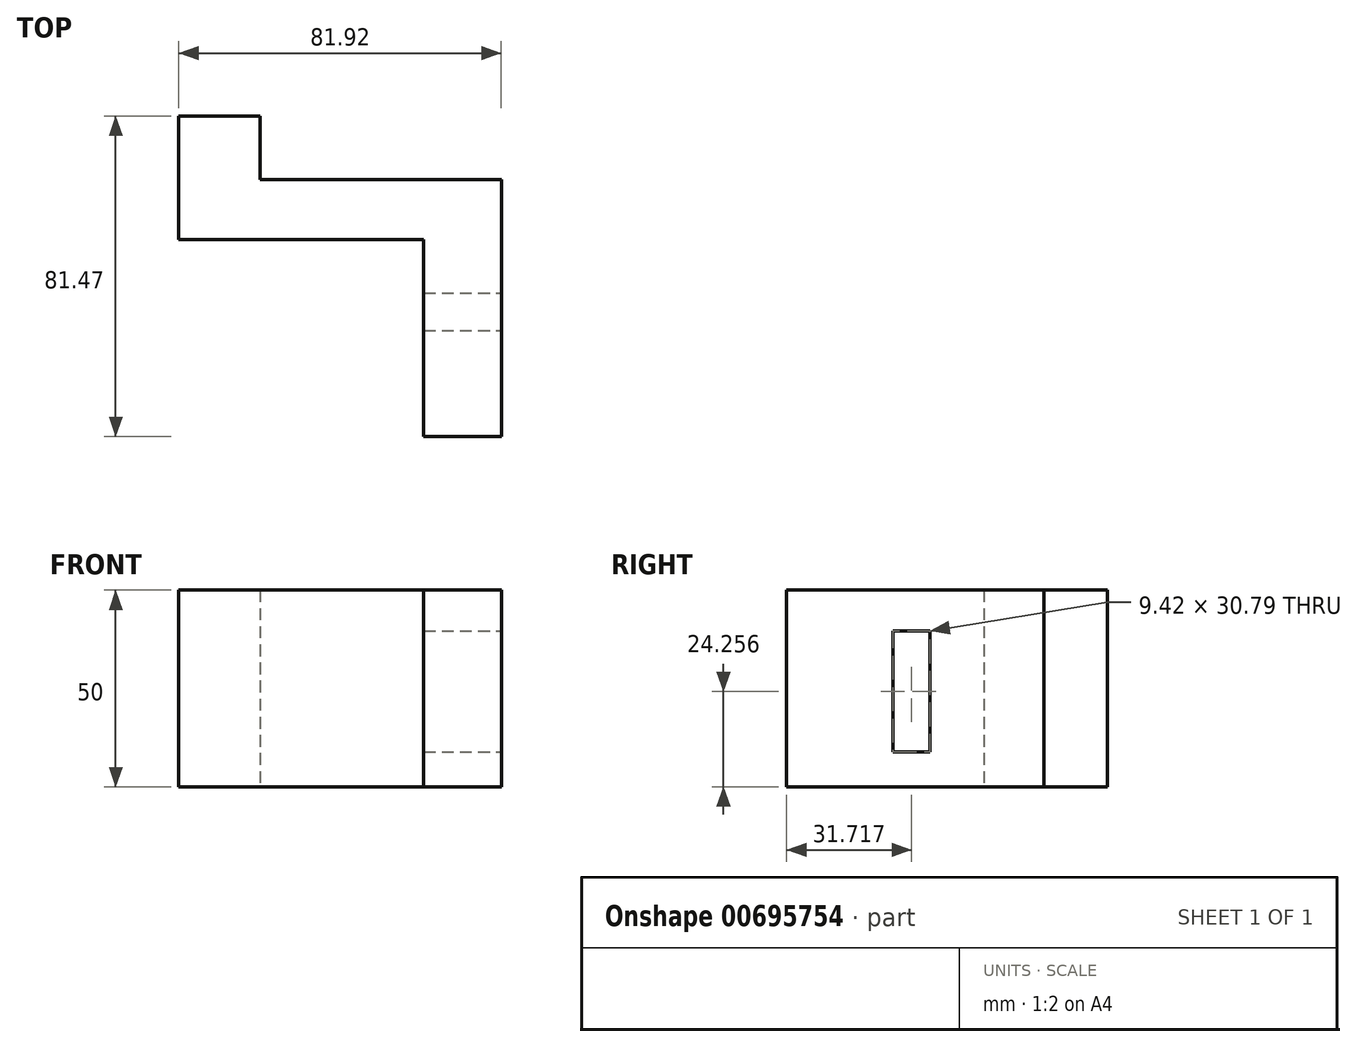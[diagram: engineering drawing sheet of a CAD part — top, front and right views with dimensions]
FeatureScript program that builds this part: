
annotation { "Feature Type Name" : "Feature", "Feature Type Description" : "" }
export const myFeature = defineFeature(function(context is Context, id is Id, definition is map)
    precondition{}
    {
        {
            var Q0;
            Q0=qCreatedBy(makeId("Top.planeOp"),FACE);
            var sketch = newSketch(context, id + "F0", { "sketchPlane" : qUnion([Q0])});
            skLineSegment(sketch, "E0", {"start": v(-119.75, 51.03) * mm, "end": v(-99.16, 51.03) * mm});
            skLineSegment(sketch, "E1", {"start": v(-99.16, 51.03) * mm, "end": v(-99.16, 34.92) * mm});
            skLineSegment(sketch, "E2", {"start": v(-119.75, 51.03) * mm, "end": v(-119.75, 19.7) * mm});
            skLineSegment(sketch, "E3", {"start": v(-119.75, 19.7) * mm, "end": v(-57.52, 19.7) * mm});
            skLineSegment(sketch, "E4", {"start": v(-57.52, 19.7) * mm, "end": v(-57.52, -30.44) * mm});
            skLineSegment(sketch, "E5", {"start": v(-57.52, -30.44) * mm, "end": v(-37.83, -30.44) * mm});
            skLineSegment(sketch, "E6", {"start": v(-37.83, -30.44) * mm, "end": v(-37.83, 34.92) * mm});
            skLineSegment(sketch, "E7", {"start": v(-37.83, 34.92) * mm, "end": v(-99.16, 34.92) * mm});
            skSolve(sketch);
        }
        {
            var Q0;
            Q0 = qSketchRegion(id + "F0", true);
            extrude(context, id + "F1", {"entities" : qUnion([Q0]), "depth" : 50 * mm, "offsetDistance" : 25 * mm});
        }
        {
            var Q0;
            Q0=makeQuery(id+"F1.opExtrude","SWEPT_FACE",FACE,{"disambiguationData":[OSD([sQuery(id+"F0.wireOp",EDGE,"E6")])]});
            var sketch = newSketch(context, id + "F2", { "sketchPlane" : qUnion([Q0])});
            skLineSegment(sketch, "E8.bottom", {"start": v(5.99, 39.65) * mm, "end": v(-3.43, 39.65) * mm});
            skLineSegment(sketch, "E8.top", {"start": v(5.99, 8.86) * mm, "end": v(-3.43, 8.86) * mm});
            skLineSegment(sketch, "E8.left", {"start": v(5.99, 39.65) * mm, "end": v(5.99, 8.86) * mm});
            skLineSegment(sketch, "E8.right", {"start": v(-3.43, 39.65) * mm, "end": v(-3.43, 8.86) * mm});
            skSolve(sketch);
        }
        {
            var Q0;
            Q0=makeQuery(id+"F2.imprint","IMPRINT",FACE,{"disambiguationData":[TD([[makeQuery(id+"F2.imprint","IMPRINT",EDGE,{"derivedFrom":sQuery(id+"F2.wireOp",EDGE,"E8.bottom")}),1.0]])]});
            extrude(context, id + "F3", {"entities" : qUnion([Q0]), "operationType" : NewBodyOperationType.REMOVE, "oppositeDirection" : true, "depth" : 25 * mm, "offsetDistance" : 25 * mm});
        }
    });
